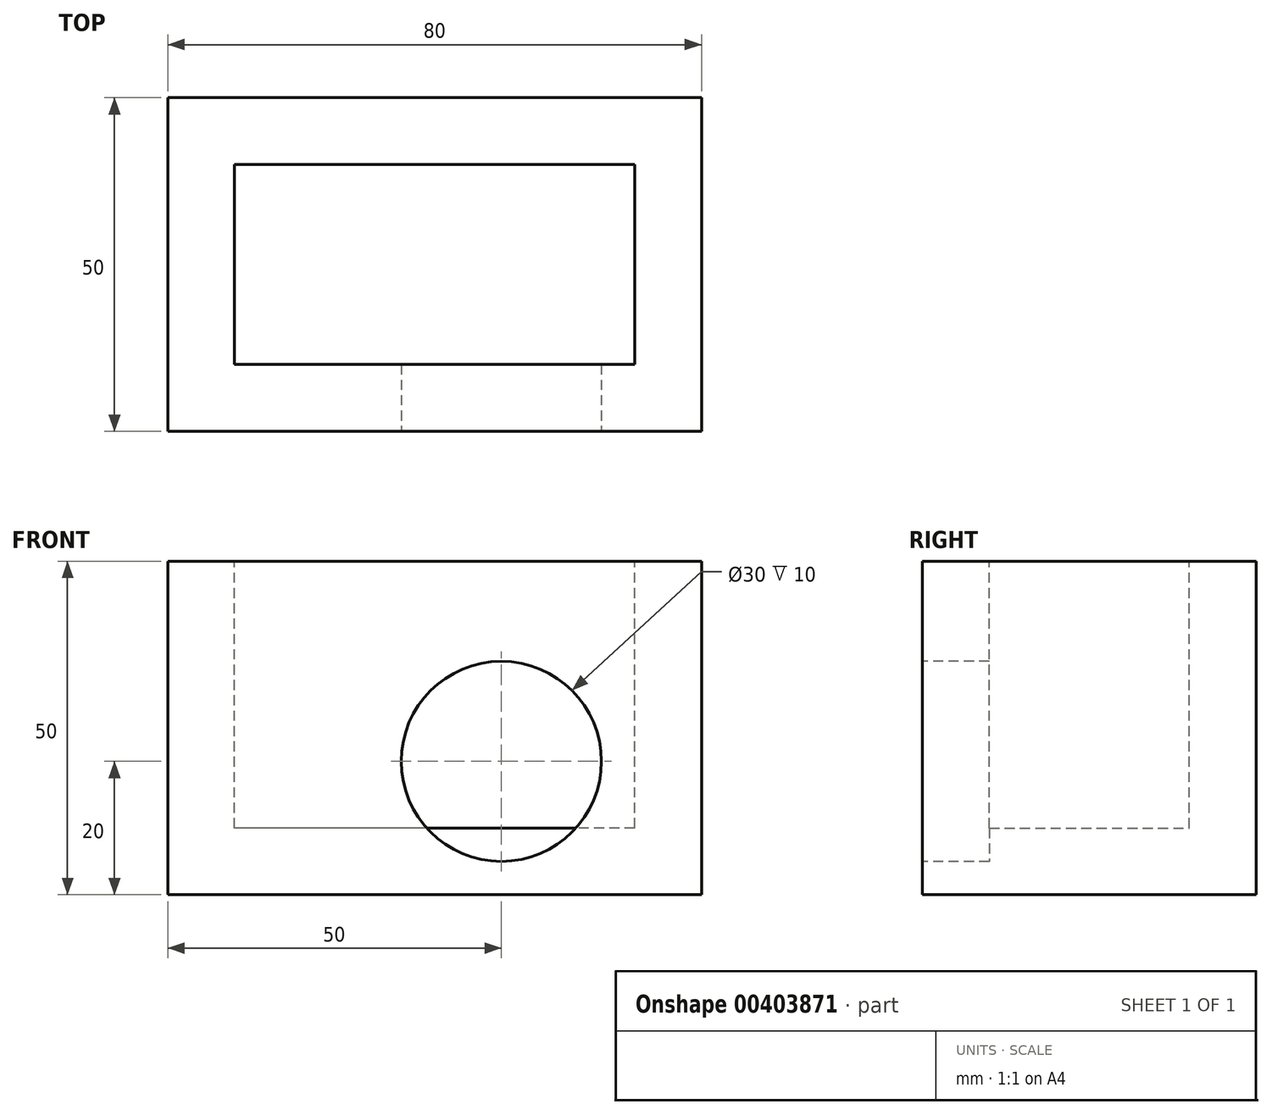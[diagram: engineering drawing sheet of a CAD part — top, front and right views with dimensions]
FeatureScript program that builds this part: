
annotation { "Feature Type Name" : "Feature", "Feature Type Description" : "" }
export const myFeature = defineFeature(function(context is Context, id is Id, definition is map)
    precondition{}
    {
        {
            var Q0;
            Q0=qCreatedBy(makeId("Top.planeOp"),FACE);
            var sketch = newSketch(context, id + "F0", { "sketchPlane" : qUnion([Q0])});
            skLineSegment(sketch, "E0.bottom", {"start": v(40, -25) * mm, "end": v(-40, -25) * mm});
            skLineSegment(sketch, "E0.top", {"start": v(40, 25) * mm, "end": v(-40, 25) * mm});
            skLineSegment(sketch, "E0.left", {"start": v(40, -25) * mm, "end": v(40, 25) * mm});
            skLineSegment(sketch, "E0.right", {"start": v(-40, -25) * mm, "end": v(-40, 25) * mm});
            skPoint(sketch, "E0.middle", {"position": v(0, 0) * mm});
            skSolve(sketch);
        }
        {
            var Q0;
            Q0 = qSketchRegion(id + "F0", true);
            extrude(context, id + "F1", {"entities" : qUnion([Q0]), "depth" : 50 * mm});
        }
        {
            var Q0;
            Q0=makeQuery(id+"F1.opExtrude","CAP_FACE",FACE,{"disambiguationData":[OSD([sQuery(id+"F0.wireOp",EDGE,"E0.bottom"),sQuery(id+"F0.wireOp",EDGE,"E0.top"),sQuery(id+"F0.wireOp",EDGE,"E0.left"),sQuery(id+"F0.wireOp",EDGE,"E0.right")])],"isStart":false});
            var sketch = newSketch(context, id + "F2", { "sketchPlane" : qUnion([Q0])});
            skLineSegment(sketch, "E1.bottom", {"start": v(30, -15) * mm, "end": v(-30, -15) * mm});
            skLineSegment(sketch, "E1.top", {"start": v(30, 15) * mm, "end": v(-30, 15) * mm});
            skLineSegment(sketch, "E1.left", {"start": v(30, -15) * mm, "end": v(30, 15) * mm});
            skLineSegment(sketch, "E1.right", {"start": v(-30, -15) * mm, "end": v(-30, 15) * mm});
            skPoint(sketch, "E1.middle", {"position": v(0, 0) * mm});
            skSolve(sketch);
        }
        {
            var Q0;
            Q0 = qSketchRegion(id + "F2", true);
            var Q1;
            Q1=makeQuery(id+"F1.opExtrude","CAP_FACE",FACE,{"disambiguationData":[OSD([sQuery(id+"F0.wireOp",EDGE,"E0.bottom"),sQuery(id+"F0.wireOp",EDGE,"E0.top"),sQuery(id+"F0.wireOp",EDGE,"E0.left"),sQuery(id+"F0.wireOp",EDGE,"E0.right")])],"isStart":true});
            extrude(context, id + "F3", {"entities" : qUnion([Q0]), "operationType" : NewBodyOperationType.REMOVE, "oppositeDirection" : true, "endBoundEntityFace" : qUnion([Q1]), "depth" : 40 * mm});
        }
        {
            var Q0;
            Q0=makeQuery(id+"F1.opExtrude","SWEPT_FACE",FACE,{"disambiguationData":[OSD([sQuery(id+"F0.wireOp",EDGE,"E0.bottom")])]});
            var sketch = newSketch(context, id + "F4", { "sketchPlane" : qUnion([Q0])});
            skLineSegment(sketch, "E2", {"start": v(10, 50) * mm, "end": v(10, 20) * mm, "construction": true});
            skCircle(sketch, "E3", {"center": v(10, 20) * mm, "radius": 15 * mm});
            skSolve(sketch);
        }
        {
            var Q0;
            Q0 = qSketchRegion(id + "F4", true);
            var Q1;
            Q1=makeQuery(id+"F3.boolean.opBoolean","COPY",FACE,{"derivedFrom":makeQuery(id+"F3.opExtrude","SWEPT_FACE",FACE,{"disambiguationData":[OSD([sQuery(id+"F2.wireOp",EDGE,"E1.bottom")])]})});
            extrude(context, id + "F5", {"entities" : qUnion([Q0]), "operationType" : NewBodyOperationType.REMOVE, "endBound" : BoundingType.UP_TO_SURFACE, "oppositeDirection" : true, "endBoundEntityFace" : qUnion([Q1]), "depth" : 25 * mm});
        }
    });
